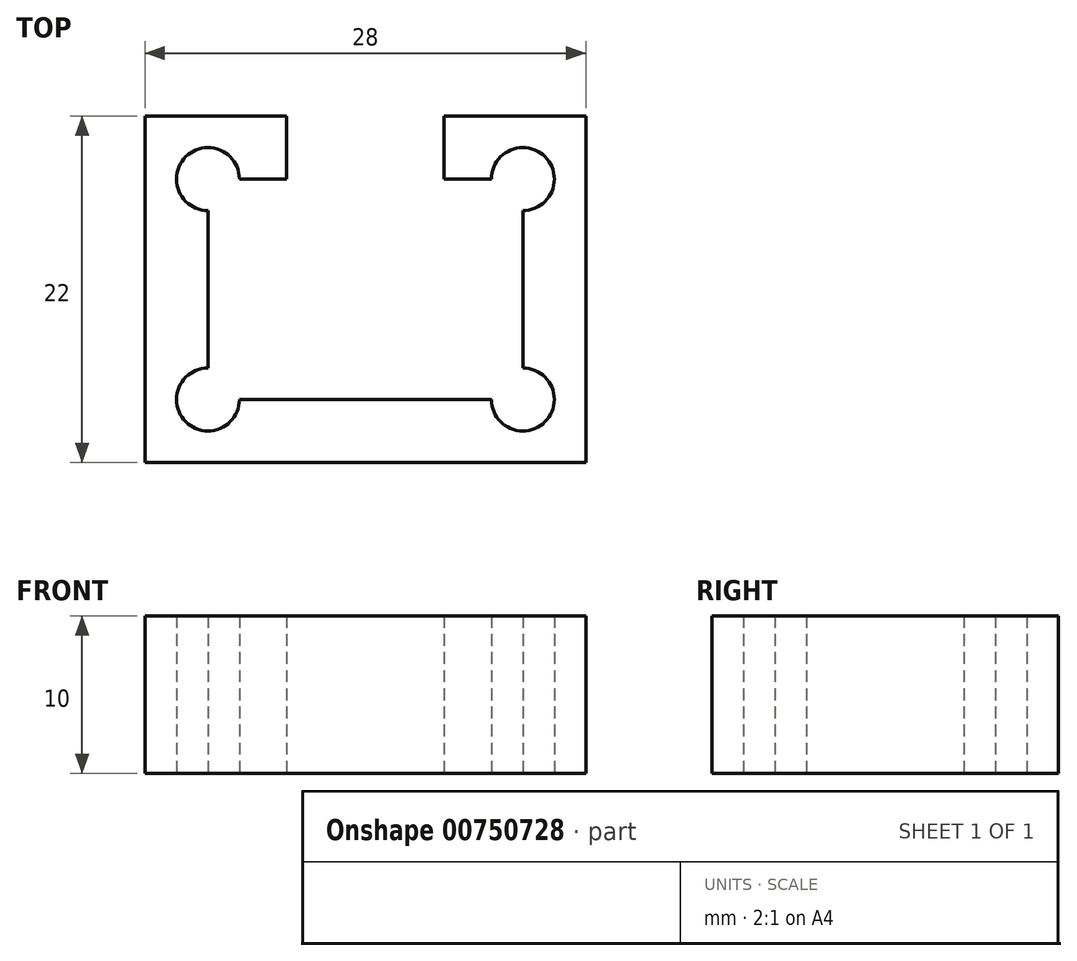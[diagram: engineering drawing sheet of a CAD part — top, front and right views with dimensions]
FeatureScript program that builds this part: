
annotation { "Feature Type Name" : "Feature", "Feature Type Description" : "" }
export const myFeature = defineFeature(function(context is Context, id is Id, definition is map)
    precondition{}
    {
        {
            var Q0;
            Q0=qCreatedBy(makeId("Top.planeOp"),FACE);
            var sketch = newSketch(context, id + "F0", { "sketchPlane" : qUnion([Q0])});
            skLineSegment(sketch, "E0.bottom", {"start": v(10, -7) * mm, "end": v(-10, -7) * mm});
            skLineSegment(sketch, "E0.top", {"start": v(10, 7) * mm, "end": v(5, 7) * mm});
            skLineSegment(sketch, "E0.left", {"start": v(10, -7) * mm, "end": v(10, 7) * mm});
            skLineSegment(sketch, "E0.right", {"start": v(-10, -7) * mm, "end": v(-10, 7) * mm});
            skPoint(sketch, "E0.middle", {"position": v(0, 0) * mm});
            skLineSegment(sketch, "E1.0", {"start": v(-14, -11) * mm, "end": v(-14, 11) * mm});
            skLineSegment(sketch, "E1.1", {"start": v(14, -11) * mm, "end": v(-14, -11) * mm});
            skLineSegment(sketch, "E1.2", {"start": v(14, -11) * mm, "end": v(14, 11) * mm});
            skLineSegment(sketch, "E1.3", {"start": v(14, 11) * mm, "end": v(5, 11) * mm});
            skLineSegment(sketch, "E2", {"start": v(-5, 11) * mm, "end": v(-5, 7) * mm});
            skLineSegment(sketch, "E3", {"start": v(5, 11) * mm, "end": v(5, 7) * mm});
            skLineSegment(sketch, "E4", {"start": v(-5, 9) * mm, "end": v(5, 9) * mm, "construction": true});
            skPoint(sketch, "E5", {"position": v(0, 9) * mm});
            skLineSegment(sketch, "E6", {"start": v(-5, 11) * mm, "end": v(-14, 11) * mm});
            skLineSegment(sketch, "E7", {"start": v(5, 11) * mm, "end": v(-5, 11) * mm, "construction": true});
            skLineSegment(sketch, "E8", {"start": v(5, 7) * mm, "end": v(-5, 7) * mm, "construction": true});
            skLineSegment(sketch, "E9", {"start": v(-5, 7) * mm, "end": v(-10, 7) * mm});
            skSolve(sketch);
        }
        {
            var Q0;
            Q0 = qSketchRegion(id + "F0", true);
            extrude(context, id + "F1", {"entities" : qUnion([Q0]), "depth" : 10 * mm, "offsetDistance" : 25 * mm});
        }
        {
            var Q0;
            Q0=qCreatedBy(makeId("Top.planeOp"),FACE);
            var sketch = newSketch(context, id + "F2", { "sketchPlane" : qUnion([Q0])});
            skLineSegment(sketch, "E10.0", {"start": v(-10, -7) * mm, "end": v(-10, 7) * mm});
            skLineSegment(sketch, "E10.1", {"start": v(-5, 7) * mm, "end": v(-10, 7) * mm});
            skLineSegment(sketch, "E10.2", {"start": v(10, 7) * mm, "end": v(5, 7) * mm});
            skLineSegment(sketch, "E10.3", {"start": v(10, -7) * mm, "end": v(10, 7) * mm});
            skLineSegment(sketch, "E10.4", {"start": v(10, -7) * mm, "end": v(-10, -7) * mm});
            skCircle(sketch, "E11", {"center": v(-10, 7) * mm, "radius": 2 * mm});
            skCircle(sketch, "E12", {"center": v(10, 7) * mm, "radius": 2 * mm});
            skCircle(sketch, "E13", {"center": v(10, -7) * mm, "radius": 2 * mm});
            skCircle(sketch, "E14", {"center": v(-10, -7) * mm, "radius": 2 * mm});
            skSolve(sketch);
        }
        {
            var Q0;
            Q0 = qSketchRegion(id + "F2", true);
            extrude(context, id + "F3", {"entities" : qUnion([Q0]), "operationType" : NewBodyOperationType.REMOVE, "endBound" : BoundingType.THROUGH_ALL, "depth" : 25 * mm, "offsetDistance" : 25 * mm});
        }
    });
